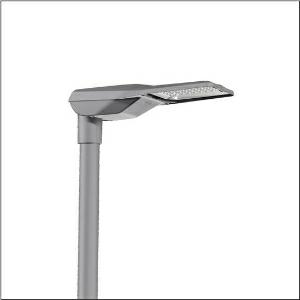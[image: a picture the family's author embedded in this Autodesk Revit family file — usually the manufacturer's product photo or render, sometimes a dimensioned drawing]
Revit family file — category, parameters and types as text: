
# Revit family: streetlight_sl_21_iq_mini___st1_0a_5xe2d21g08hb_8dd2
name_source: partatom
category: Lighting Fixtures
units: mm (PartAtom-declared; Revit-internal decimal feet)

## family parameters
Cut with Voids When Loaded = No
Host = Face
Light Source = No
Part Type = Normal
Room Calculation Point = No
Round Connector Dimension = Use Diameter
Shared = No

## types (1)
- --- (1 x LED, 7830 lm, 70.9 W, 2200K)
    Apparent Load = 71 VA
    CIE Flux Codes = 37 72 97 100 100
    Color Rendering = 70
    Color Temperature = 2200K
    Default Elevation = 1800 mm
    Description = Streetlight SL 21 mini, mast luminaire, primary light control with lens, of PMMA, primary optical cover: cover, of toughened safety glass, transparent, light distribution: ST1.0a, light emission: direct distribution, primary light characteristic: asymmetric, installation type: post-top, side-entry, LED, High Power LED, rated luminous flux: 7.830lm, luminous efficacy: 110lm/W, light colour: 722, colour temperature: 2200K, control gear: ECG iQ, control: Street-Remote, Auto-Match, Temp-Guard, Lumen-Switch, Night-Set, Smart-Wire, Light-Fading, Desk-Remote (wireless, voltage-free reading and setting of iQ features in the workshop via application-optimized NFC function/RFID function), optimised constant luminous flux control (CLO 2.0), mains connection: 220..240V, AC, 50/60Hz, start of lifetime: 71W, end of lifetime: 75W, reduction: 31W, luminaire housing, of diecast aluminium, powder-coated, Siteco® metallic grey (DB 702S), corrosivity category C5 according to DIN EN ISO 12944, length: 628mm, width: 235mm, height: 110mm, spigot size: 60/76mm (post-top) and 42/60/76mm (side-entry), mast flange for spigot size: 42mm: 5XC10008XM4, 60mm: 5XC10008XM2, 76/60mm: 5XC10108XM1, protection rating (complete): IP66, insulation class (complete): insulation class II (safety insulation), certification: CE, ENEC, VDE, impact resistance: IK09, permissible operating ambient temperature for outdoor applications: -40..+50°C, standard-compliant lighting for roads and squares, packaging unit: 1 piece

Light Distribution: ST1.0a
    Height = 110 mm
    Lamp = 1 x LED
    Lamp Light Flux = 7830 lm
    Lamp Power = 70.9 W
    Lamp count = 1
    Length = 625 mm
    Luminous efficacy = 110 lm/W
    Manufacturer = Siteco
    ModVariant = No
    Model = 5XE2D21G08HB
    Number of Poles = 1
    OnlyDefault = Yes
    Power Factor = 1
    Product Name = Streetlight SL 21 iQ mini | ST1.0a
    Product group = mast luminaire | pylon top
    ProductGroupID = 6100
    Protection Class = Protection class II
    Protection Degree = IP 66
    RLX_Detail_Level = 1
    RlxData = <blob elided: 92789 chars, md5=03d7e57c>
    Socket = socket
    Standby Power = 0 W
    System Light Flux = 7830 lm
    System Power = 71 W
    Type Comments = factory setting: luminous flux: 100 % | dim-lin: 254 | 711 mA
    Type Image = l_1003519.jpg
    URL = http://relux.com
    VarID = @adj_069531
    Voltage = 0 V
    Weight = 0.00 kg
    Width = 234 mm

## geometry (parser evidence)
native form markers: Blend x4, Sweep x11
no freeform markers — native parametric forms only
